# Revit family: GSV4-4in-Flanged-Gas-Solenoid-Valve
name_source: partatom
category: Pipe Accessories
units: mm (PartAtom-declared; Revit-internal decimal feet)

## family parameters
Always vertical = Yes
Cut with Voids When Loaded = No
Part Type = Valve - Breaks Into
Round Connector Dimension = Use Diameter
Shared = No
Work Plane-Based = No

## types (1)
- GSV4-4in-Flanged-Gas-Solenoid-Valve
    Ambient temperature rating = -40°F to +150°F (-40°C to +66°C)
    Amperage = 0.94
    Cf/h = 10200
    Closing Time = One Second Maximum
    Cu m/hr = 288.8
    Default Elevation = 0"
    Description = AGS gas solenoid valves control the flow of natural and LP (liquefied petroleum) gases and are most commonly used in with our range of
utility controllers and gas detection systems. Designed for ON/OFF service.
    Full Load = 9.8A FOR 120V & 4.9A FOR 240V
    Inrush = 3.9
    Locked Rotor = 58.8A FOR 120V & 29.4A FOR 240V
    Manufacturer = American Gas Safety LLC
    Max Operating Pressure Differential = 3 PSI
    Max. Rated Pressure = 15PSI
    Model = AGSGSV4
    Nominal Opening Time = 16 Seconds at 50Hz
    Pipe Dia = 4"
    Tel = (727) 608-4375
    URL = https://americangassafety.com
    VA = 115
    Volt = 120VAC / 60Hz
    Wattage = 50.0

## geometry (parser evidence)
native form markers: Sweep x3
no freeform markers — native parametric forms only
